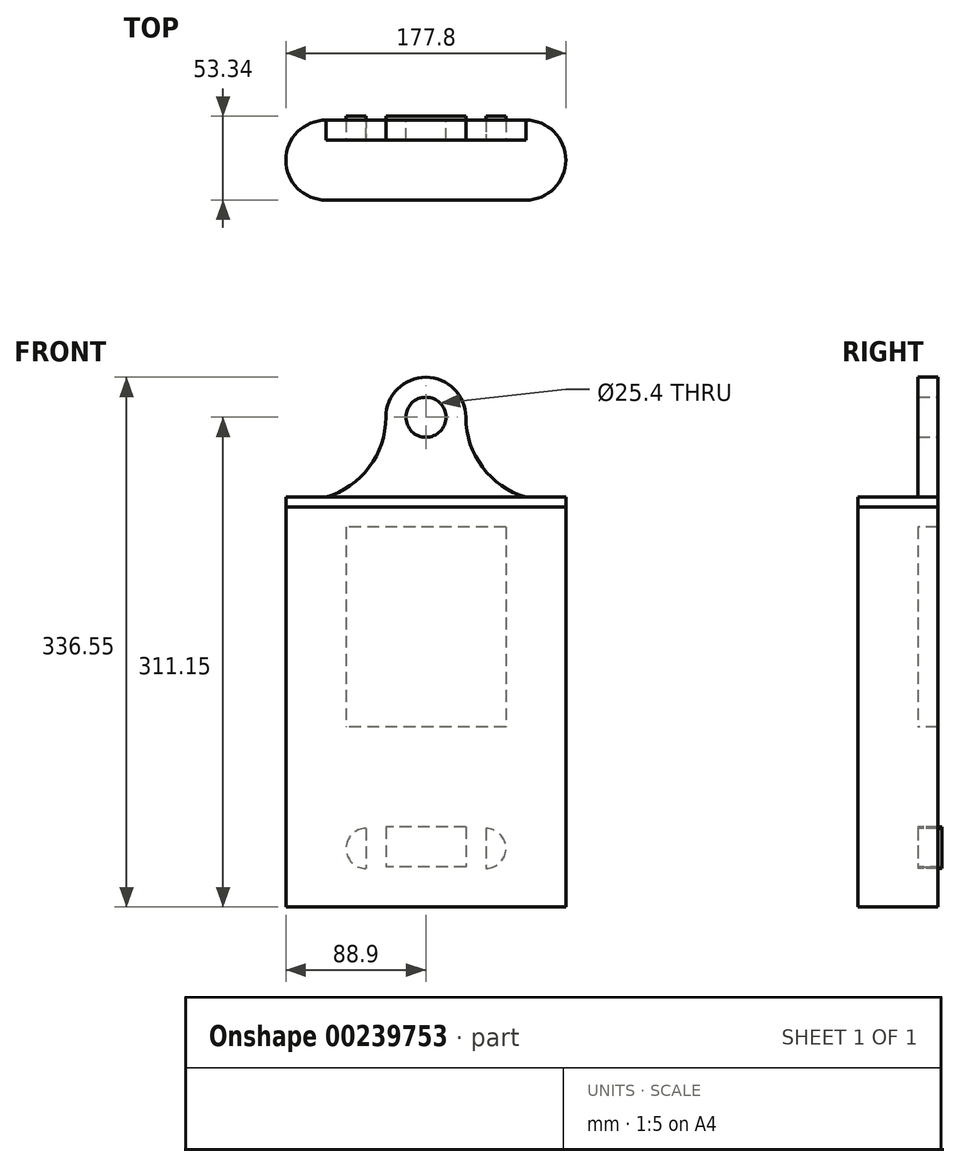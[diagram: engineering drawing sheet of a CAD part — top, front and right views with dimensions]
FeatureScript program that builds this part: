
annotation { "Feature Type Name" : "Feature", "Feature Type Description" : "" }
export const myFeature = defineFeature(function(context is Context, id is Id, definition is map)
    precondition{}
    {
        {
            var Q0;
            Q0=qCreatedBy(makeId("Top.planeOp"),FACE);
            var sketch = newSketch(context, id + "F0", { "sketchPlane" : qUnion([Q0])});
            skLineSegment(sketch, "E0.bottom", {"start": v(88.9, 25.4) * mm, "end": v(-88.9, 25.4) * mm});
            skLineSegment(sketch, "E0.top", {"start": v(88.9, -25.4) * mm, "end": v(-88.9, -25.4) * mm});
            skLineSegment(sketch, "E0.left", {"start": v(88.9, 25.4) * mm, "end": v(88.9, -25.4) * mm});
            skLineSegment(sketch, "E0.right", {"start": v(-88.9, 25.4) * mm, "end": v(-88.9, -25.4) * mm});
            skPoint(sketch, "E0.middle", {"position": v(0, 0) * mm});
            skSolve(sketch);
        }
        {
            var Q0;
            Q0 = qSketchRegion(id + "F0", true);
            extrude(context, id + "F1", {"entities" : qUnion([Q0]), "endBound" : BoundingType.SYMMETRIC, "depth" : 254 * mm});
        }
        {
            var Q0;
            Q0=makeQuery(id+"F1.opExtrude","SWEPT_EDGE",EDGE,{"disambiguationData":[OSD([sQuery(id+"F0.wireOp",EDGE,"E0.top"),sQuery(id+"F0.wireOp",EDGE,"E0.right")])]});
            var Q1;
            Q1=makeQuery(id+"F1.opExtrude","SWEPT_EDGE",EDGE,{"disambiguationData":[OSD([sQuery(id+"F0.wireOp",EDGE,"E0.bottom"),sQuery(id+"F0.wireOp",EDGE,"E0.right")])]});
            var Q2;
            Q2=makeQuery(id+"F1.opExtrude","SWEPT_EDGE",EDGE,{"disambiguationData":[OSD([sQuery(id+"F0.wireOp",EDGE,"E0.top"),sQuery(id+"F0.wireOp",EDGE,"E0.left")])]});
            var Q3;
            Q3=makeQuery(id+"F1.opExtrude","SWEPT_EDGE",EDGE,{"disambiguationData":[OSD([sQuery(id+"F0.wireOp",EDGE,"E0.bottom"),sQuery(id+"F0.wireOp",EDGE,"E0.left")])]});
            fillet(context, id + "F2", {"entities" : qUnion([Q0, Q1, Q2, Q3]), "radius" : 25.4 * mm, "tangentPropagation" : true, "allowEdgeOverflow" : false});
        }
        {
            var Q0;
            Q0=makeQuery(id+"F1.opExtrude","SWEPT_FACE",FACE,{"disambiguationData":[OSD([sQuery(id+"F0.wireOp",EDGE,"E0.bottom")])]});
            var sketch = newSketch(context, id + "F3", { "sketchPlane" : qUnion([Q0])});
            skLineSegment(sketch, "E1.bottom", {"start": v(-50.8, 114.3) * mm, "end": v(50.8, 114.3) * mm});
            skLineSegment(sketch, "E1.top", {"start": v(-50.8, -12.7) * mm, "end": v(50.8, -12.7) * mm});
            skLineSegment(sketch, "E1.left", {"start": v(-50.8, 114.3) * mm, "end": v(-50.8, -12.7) * mm});
            skLineSegment(sketch, "E1.right", {"start": v(50.8, 114.3) * mm, "end": v(50.8, -12.7) * mm});
            skLineSegment(sketch, "E2.bottom", {"start": v(-25.4, -76.2) * mm, "end": v(25.4, -76.2) * mm});
            skLineSegment(sketch, "E2.top", {"start": v(-25.4, -101.6) * mm, "end": v(25.4, -101.6) * mm});
            skLineSegment(sketch, "E2.left", {"start": v(-25.4, -76.2) * mm, "end": v(-25.4, -101.6) * mm});
            skLineSegment(sketch, "E2.right", {"start": v(25.4, -76.2) * mm, "end": v(25.4, -101.6) * mm});
            skLineSegment(sketch, "E3", {"start": v(-38.1, -77.07) * mm, "end": v(-38.1, -102.47) * mm});
            skArc(sketch, "E4", {"start": v(-38.1, -77.07) * mm, "mid": v(-50.8, -89.77) * mm, "end": v(-38.1, -102.47) * mm});
            skArc(sketch, "E5.MirrorCS", {"start": v(38.1, -77.07) * mm, "mid": v(50.8, -89.77) * mm, "end": v(38.1, -102.47) * mm});
            skLineSegment(sketch, "E6.MirrorCS", {"start": v(38.1, -77.07) * mm, "end": v(38.1, -102.47) * mm});
            skSolve(sketch);
        }
        {
            var Q0;
            Q0 = qSketchRegion(id + "F3", true);
            extrude(context, id + "F4", {"entities" : qUnion([Q0]), "operationType" : NewBodyOperationType.REMOVE, "oppositeDirection" : true, "depth" : 12.7 * mm});
        }
        {
            var Q0;
            Q0=makeQuery(id+"F4.boolean.opBoolean","COPY",FACE,{"derivedFrom":makeQuery(id+"F4.opExtrude","CAP_FACE",FACE,{"disambiguationData":[OSD([sQuery(id+"F3.wireOp",EDGE,"E3"),sQuery(id+"F3.wireOp",EDGE,"E4")])],"isStart":false})});
            extrude(context, id + "F5", {"entities" : qUnion([Q0]), "depth" : 15.24 * mm});
        }
        {
            var Q0;
            Q0=makeQuery(id+"F4.boolean.opBoolean","COPY",FACE,{"derivedFrom":makeQuery(id+"F4.opExtrude","CAP_FACE",FACE,{"disambiguationData":[OSD([sQuery(id+"F3.wireOp",EDGE,"E2.bottom"),sQuery(id+"F3.wireOp",EDGE,"E2.top"),sQuery(id+"F3.wireOp",EDGE,"E2.left"),sQuery(id+"F3.wireOp",EDGE,"E2.right")])],"isStart":false})});
            extrude(context, id + "F6", {"entities" : qUnion([Q0]), "depth" : 15.24 * mm});
        }
        {
            var Q0;
            Q0=makeQuery(id+"F4.boolean.opBoolean","COPY",FACE,{"derivedFrom":makeQuery(id+"F4.opExtrude","CAP_FACE",FACE,{"disambiguationData":[OSD([sQuery(id+"F3.wireOp",EDGE,"E5.MirrorCS"),sQuery(id+"F3.wireOp",EDGE,"E6.MirrorCS")])],"isStart":false})});
            extrude(context, id + "F7", {"entities" : qUnion([Q0]), "depth" : 15.24 * mm});
        }
        {
            var Q0;
            Q0=makeQuery(id+"F4.boolean.opBoolean","COPY",FACE,{"derivedFrom":makeQuery(id+"F4.opExtrude","CAP_FACE",FACE,{"disambiguationData":[OSD([sQuery(id+"F3.wireOp",EDGE,"E1.bottom"),sQuery(id+"F3.wireOp",EDGE,"E1.top"),sQuery(id+"F3.wireOp",EDGE,"E1.left"),sQuery(id+"F3.wireOp",EDGE,"E1.right")])],"isStart":false})});
            extrude(context, id + "F8", {"entities" : qUnion([Q0]), "depth" : 12.7 * mm});
        }
        {
            var Q0;
            Q0=makeQuery(id+"F1.opExtrude","SWEPT_FACE",FACE,{"disambiguationData":[OSD([sQuery(id+"F0.wireOp",EDGE,"E0.bottom")])]});
            var sketch = newSketch(context, id + "F9", { "sketchPlane" : qUnion([Q0])});
            skLineSegment(sketch, "E7", {"start": v(-63.5, 127) * mm, "end": v(63.5, 127) * mm});
            skLineSegment(sketch, "E8.bottom", {"start": v(-88.9, 127) * mm, "end": v(88.9, 127) * mm});
            skLineSegment(sketch, "E8.top", {"start": v(-88.9, 133.35) * mm, "end": v(-63.5, 133.35) * mm});
            skLineSegment(sketch, "E8.left", {"start": v(-88.9, 127) * mm, "end": v(-88.9, 133.35) * mm});
            skLineSegment(sketch, "E8.right", {"start": v(88.9, 127) * mm, "end": v(88.9, 133.35) * mm});
            skLineSegment(sketch, "E9.bottom", {"start": v(25.4, 133.35) * mm, "end": v(-25.4, 133.35) * mm});
            skLineSegment(sketch, "E9.top", {"start": v(25.4, 184.15) * mm, "end": v(-25.4, 184.15) * mm});
            skLineSegment(sketch, "E9.left", {"start": v(25.4, 133.35) * mm, "end": v(25.4, 184.15) * mm});
            skLineSegment(sketch, "E9.right", {"start": v(-25.4, 133.35) * mm, "end": v(-25.4, 184.15) * mm});
            skLineSegment(sketch, "E10", {"start": v(63.5, 133.35) * mm, "end": v(88.9, 133.35) * mm});
            skLineSegment(sketch, "E11", {"start": v(-63.5, 133.35) * mm, "end": v(-25.4, 133.35) * mm});
            skArc(sketch, "E12", {"start": v(25.4, 184.15) * mm, "mid": v(35.98, 152.4) * mm, "end": v(63.5, 133.35) * mm});
            skArc(sketch, "E13", {"start": v(-63.5, 133.35) * mm, "mid": v(-35.98, 152.4) * mm, "end": v(-25.4, 184.15) * mm});
            skArc(sketch, "E14", {"start": v(25.4, 184.15) * mm, "mid": v(0, 209.55) * mm, "end": v(-25.4, 184.15) * mm});
            skLineSegment(sketch, "E15", {"start": v(25.4, 133.35) * mm, "end": v(63.5, 133.35) * mm});
            skLineSegment(sketch, "E16", {"start": v(-25.4, 133.35) * mm, "end": v(25.4, 133.35) * mm});
            skCircle(sketch, "E17", {"center": v(0, 184.15) * mm, "radius": 12.7 * mm});
            skSolve(sketch);
        }
        {
            var Q0;
            Q0=makeQuery(id+"F9.imprint","IMPRINT",FACE,{"disambiguationData":[TD([[makeQuery(id+"F9.imprint","IMPRINT",EDGE,{"derivedFrom":sQuery(id+"F9.wireOp",EDGE,"E8.top")}),-1.0]])]});
            extrude(context, id + "F10", {"entities" : qUnion([Q0]), "oppositeDirection" : true, "depth" : 50.8 * mm});
        }
        {
            var Q0;
            {var subQ1=sQuery(id+"F9.wireOp",EDGE,"E9.left");Q0=makeQuery(id+"F9.imprint","IMPRINT",FACE,{"disambiguationData":[TD([[makeQuery(id+"F9.imprint","IMPRINT",EDGE,{"derivedFrom":subQ1}),1.0]])]});}
            var Q1;
            Q1=makeQuery(id+"F9.imprint","IMPRINT",FACE,{"disambiguationData":[TD([[makeQuery(id+"F9.imprint","IMPRINT",EDGE,{"derivedFrom":sQuery(id+"F9.wireOp",EDGE,"E9.left")}),-1.0]])]});
            var Q2;
            Q2=makeQuery(id+"F9.imprint","IMPRINT",FACE,{"disambiguationData":[TD([[makeQuery(id+"F9.imprint","IMPRINT",EDGE,{"derivedFrom":sQuery(id+"F9.wireOp",EDGE,"E9.right")}),1.0]])]});
            var Q3;
            {var subQ0=sQuery(id+"F9.wireOp",EDGE,"E14");Q3=makeQuery(id+"F9.imprint","IMPRINT",FACE,{"disambiguationData":[TD([[makeQuery(id+"F9.imprint","IMPRINT",EDGE,{"derivedFrom":subQ0}),1.0]])]});}
            extrude(context, id + "F11", {"entities" : qUnion([Q0, Q1, Q2, Q3]), "operationType" : NewBodyOperationType.ADD, "oppositeDirection" : true, "depth" : 12.7 * mm});
        }
        {
            var Q0;
            Q0=makeQuery(id+"F10.opExtrude","CAP_EDGE",EDGE,{"disambiguationData":[OSD([sQuery(id+"F9.wireOp",EDGE,"E8.right")])],"isStart":false});
            var Q1;
            Q1=makeQuery(id+"F10.opExtrude","CAP_EDGE",EDGE,{"disambiguationData":[OSD([sQuery(id+"F9.wireOp",EDGE,"E8.right")])],"isStart":true});
            var Q2;
            Q2=makeQuery(id+"F10.opExtrude","CAP_EDGE",EDGE,{"disambiguationData":[OSD([sQuery(id+"F9.wireOp",EDGE,"E8.left")])],"isStart":false});
            var Q3;
            Q3=makeQuery(id+"F10.opExtrude","CAP_EDGE",EDGE,{"disambiguationData":[OSD([sQuery(id+"F9.wireOp",EDGE,"E8.left")])],"isStart":true});
            fillet(context, id + "F12", {"entities" : qUnion([Q0, Q1, Q2, Q3]), "radius" : 25.4 * mm, "tangentPropagation" : true, "allowEdgeOverflow" : false});
        }
    });
